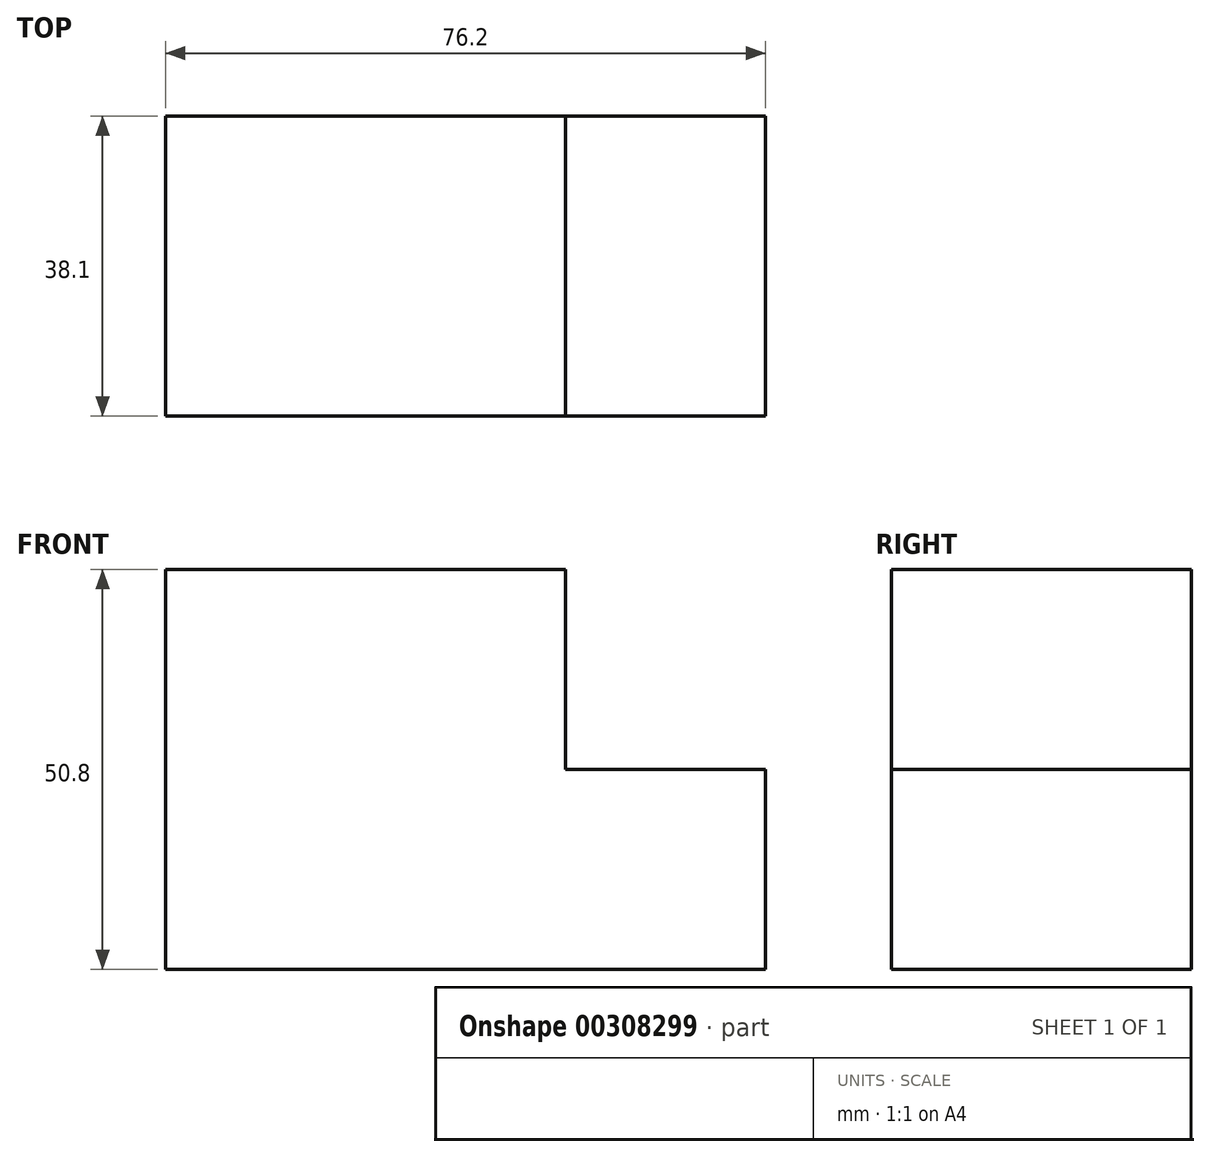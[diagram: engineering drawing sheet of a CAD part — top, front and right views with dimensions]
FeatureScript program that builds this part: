
annotation { "Feature Type Name" : "Feature", "Feature Type Description" : "" }
export const myFeature = defineFeature(function(context is Context, id is Id, definition is map)
    precondition{}
    {
        {
            var Q0;
            Q0=qCreatedBy(makeId("Front.planeOp"),FACE);
            var sketch = newSketch(context, id + "F0", { "sketchPlane" : qUnion([Q0])});
            skLineSegment(sketch, "E0", {"start": v(-35.09, -36.58) * mm, "end": v(41.11, -36.58) * mm});
            skLineSegment(sketch, "E1", {"start": v(41.11, -36.58) * mm, "end": v(41.11, -11.18) * mm});
            skLineSegment(sketch, "E2", {"start": v(41.11, -11.18) * mm, "end": v(15.71, -11.18) * mm});
            skLineSegment(sketch, "E3", {"start": v(15.71, -11.18) * mm, "end": v(15.71, 52.32) * mm});
            skLineSegment(sketch, "E4", {"start": v(15.71, 52.32) * mm, "end": v(41.11, 52.32) * mm});
            skLineSegment(sketch, "E5", {"start": v(41.11, 52.32) * mm, "end": v(41.11, 77.72) * mm});
            skLineSegment(sketch, "E6", {"start": v(41.11, 77.72) * mm, "end": v(-35.09, 77.72) * mm});
            skLineSegment(sketch, "E7", {"start": v(-35.09, 77.72) * mm, "end": v(-35.09, 52.32) * mm});
            skLineSegment(sketch, "E8", {"start": v(-35.09, 52.32) * mm, "end": v(-9.69, 52.32) * mm});
            skLineSegment(sketch, "E9", {"start": v(-9.69, 52.32) * mm, "end": v(-9.69, -11.18) * mm});
            skLineSegment(sketch, "E10", {"start": v(-9.69, -11.18) * mm, "end": v(-35.09, -11.18) * mm});
            skLineSegment(sketch, "E11", {"start": v(-35.09, -11.18) * mm, "end": v(-35.09, -36.58) * mm});
            skSolve(sketch);
        }
        {
            var Q0;
            Q0=makeQuery(id+"F0.imprint","IMPRINT",FACE,{"disambiguationData":[TD([[makeQuery(id+"F0.imprint","IMPRINT",EDGE,{"derivedFrom":sQuery(id+"F0.wireOp",EDGE,"E0")}),1.0]])]});
            extrude(context, id + "F1", {"entities" : qUnion([Q0]), "depth" : 76.2 * mm});
        }
        {
            var Q0;
            Q0=makeQuery(id+"F1.opExtrude","SWEPT_FACE",FACE,{"disambiguationData":[OSD([sQuery(id+"F0.wireOp",EDGE,"E3")])]});
            var sketch = newSketch(context, id + "F2", { "sketchPlane" : qUnion([Q0])});
            skCircle(sketch, "E12", {"center": v(-38.1, 20.57) * mm, "radius": 25.4 * mm});
            skPoint(sketch, "E12.centerSnap0", {"position": v(-38.1, 52.32) * mm});
            skPoint(sketch, "E12.centerSnap1", {"position": v(-76.2, 20.57) * mm});
            skSolve(sketch);
        }
        {
            var Q0;
            Q0=makeQuery(id+"F2.imprint","IMPRINT",FACE,{"disambiguationData":[TD([[makeQuery(id+"F2.imprint","IMPRINT",EDGE,{"derivedFrom":sQuery(id+"F2.wireOp",EDGE,"E12")}),1.0]])]});
            extrude(context, id + "F3", {"entities" : qUnion([Q0]), "operationType" : NewBodyOperationType.REMOVE, "oppositeDirection" : true, "depth" : 50.8 * mm});
        }
        {
            var Q0;
            Q0=qCreatedBy(makeId("Front.planeOp"),FACE);
            var sketch = newSketch(context, id + "F4", { "sketchPlane" : qUnion([Q0])});
            skLineSegment(sketch, "E13.bottom", {"start": v(-29.24, 71.91) * mm, "end": v(-15.59, 71.91) * mm});
            skLineSegment(sketch, "E13.top", {"start": v(-29.24, 56.77) * mm, "end": v(-15.59, 56.77) * mm});
            skLineSegment(sketch, "E13.left", {"start": v(-29.24, 71.91) * mm, "end": v(-29.24, 56.77) * mm});
            skLineSegment(sketch, "E13.right", {"start": v(-15.59, 71.91) * mm, "end": v(-15.59, 56.77) * mm});
            skPoint(sketch, "E14.firstSnap0", {"position": v(-22.41, 71.91) * mm});
            skLineSegment(sketch, "E14.bottom", {"start": v(23.6, 71.91) * mm, "end": v(36.07, 71.91) * mm});
            skLineSegment(sketch, "E14.top", {"start": v(23.6, 56.77) * mm, "end": v(36.07, 56.77) * mm});
            skLineSegment(sketch, "E14.left", {"start": v(23.6, 71.91) * mm, "end": v(23.6, 56.77) * mm});
            skLineSegment(sketch, "E14.right", {"start": v(36.07, 71.91) * mm, "end": v(36.07, 56.77) * mm});
            skLineSegment(sketch, "E15.bottom", {"start": v(-28.65, -17.44) * mm, "end": v(-15.59, -17.44) * mm});
            skLineSegment(sketch, "E15.top", {"start": v(-28.65, -31.99) * mm, "end": v(-15.59, -31.99) * mm});
            skLineSegment(sketch, "E15.left", {"start": v(-28.65, -17.44) * mm, "end": v(-28.65, -31.99) * mm});
            skLineSegment(sketch, "E15.right", {"start": v(-15.59, -17.44) * mm, "end": v(-15.59, -31.99) * mm});
            skLineSegment(sketch, "E16.bottom", {"start": v(24.2, -21.3) * mm, "end": v(39.33, -21.3) * mm});
            skLineSegment(sketch, "E16.top", {"start": v(24.2, -31.99) * mm, "end": v(39.33, -31.99) * mm});
            skLineSegment(sketch, "E16.left", {"start": v(24.2, -21.3) * mm, "end": v(24.2, -31.99) * mm});
            skLineSegment(sketch, "E16.right", {"start": v(39.33, -21.3) * mm, "end": v(39.33, -31.99) * mm});
            skCircle(sketch, "E17", {"center": v(3.3, 23.36) * mm, "radius": 11.88 * mm});
            skPoint(sketch, "E17.first.point", {"position": v(-4, 32.73) * mm});
            skPoint(sketch, "E17.second.point", {"position": v(10.24, 13.73) * mm});
            skPoint(sketch, "E17.third.point", {"position": v(-8.16, 20.26) * mm});
            skSolve(sketch);
        }
        {
            var Q0;
            Q0 = qSketchRegion(id + "F4", true);
            var Q1;
            Q1=makeQuery(id+"F1.opExtrude","CAP_FACE",FACE,{"disambiguationData":[OSD([sQuery(id+"F0.wireOp",EDGE,"E0"),sQuery(id+"F0.wireOp",EDGE,"E1"),sQuery(id+"F0.wireOp",EDGE,"E2"),sQuery(id+"F0.wireOp",EDGE,"E3"),sQuery(id+"F0.wireOp",EDGE,"E4"),sQuery(id+"F0.wireOp",EDGE,"E5"),sQuery(id+"F0.wireOp",EDGE,"E6"),sQuery(id+"F0.wireOp",EDGE,"E7"),sQuery(id+"F0.wireOp",EDGE,"E8"),sQuery(id+"F0.wireOp",EDGE,"E9"),sQuery(id+"F0.wireOp",EDGE,"E10"),sQuery(id+"F0.wireOp",EDGE,"E11")])],"isStart":false});
            extrude(context, id + "F5", {"entities" : qUnion([Q0, Q1]), "operationType" : NewBodyOperationType.REMOVE, "endBound" : BoundingType.THROUGH_ALL, "oppositeDirection" : true, "depth" : 0.5 * mm});
        }
        {
            var Q0;
            Q0=qCreatedBy(makeId("Front.planeOp"),FACE);
            var sketch = newSketch(context, id + "F6", { "sketchPlane" : qUnion([Q0])});
            skLineSegment(sketch, "E18", {"start": v(-36.68, -28.66) * mm, "end": v(39.52, -28.66) * mm});
            skLineSegment(sketch, "E19", {"start": v(39.52, -28.66) * mm, "end": v(39.52, -3.26) * mm});
            skLineSegment(sketch, "E20", {"start": v(39.52, -3.26) * mm, "end": v(14.12, -3.26) * mm});
            skLineSegment(sketch, "E21", {"start": v(14.12, -3.26) * mm, "end": v(14.12, 22.14) * mm});
            skLineSegment(sketch, "E22", {"start": v(14.12, 22.14) * mm, "end": v(-36.68, 22.14) * mm});
            skLineSegment(sketch, "E23", {"start": v(-36.68, 22.14) * mm, "end": v(-36.68, -28.66) * mm});
            skSolve(sketch);
        }
        {
            var Q0;
            Q0=makeQuery(id+"F6.imprint","IMPRINT",FACE,{"disambiguationData":[TD([[makeQuery(id+"F6.imprint","IMPRINT",EDGE,{"derivedFrom":sQuery(id+"F6.wireOp",EDGE,"E18")}),1.0]])]});
            extrude(context, id + "F7", {"entities" : qUnion([Q0]), "depth" : 38.1 * mm});
        }
    });
